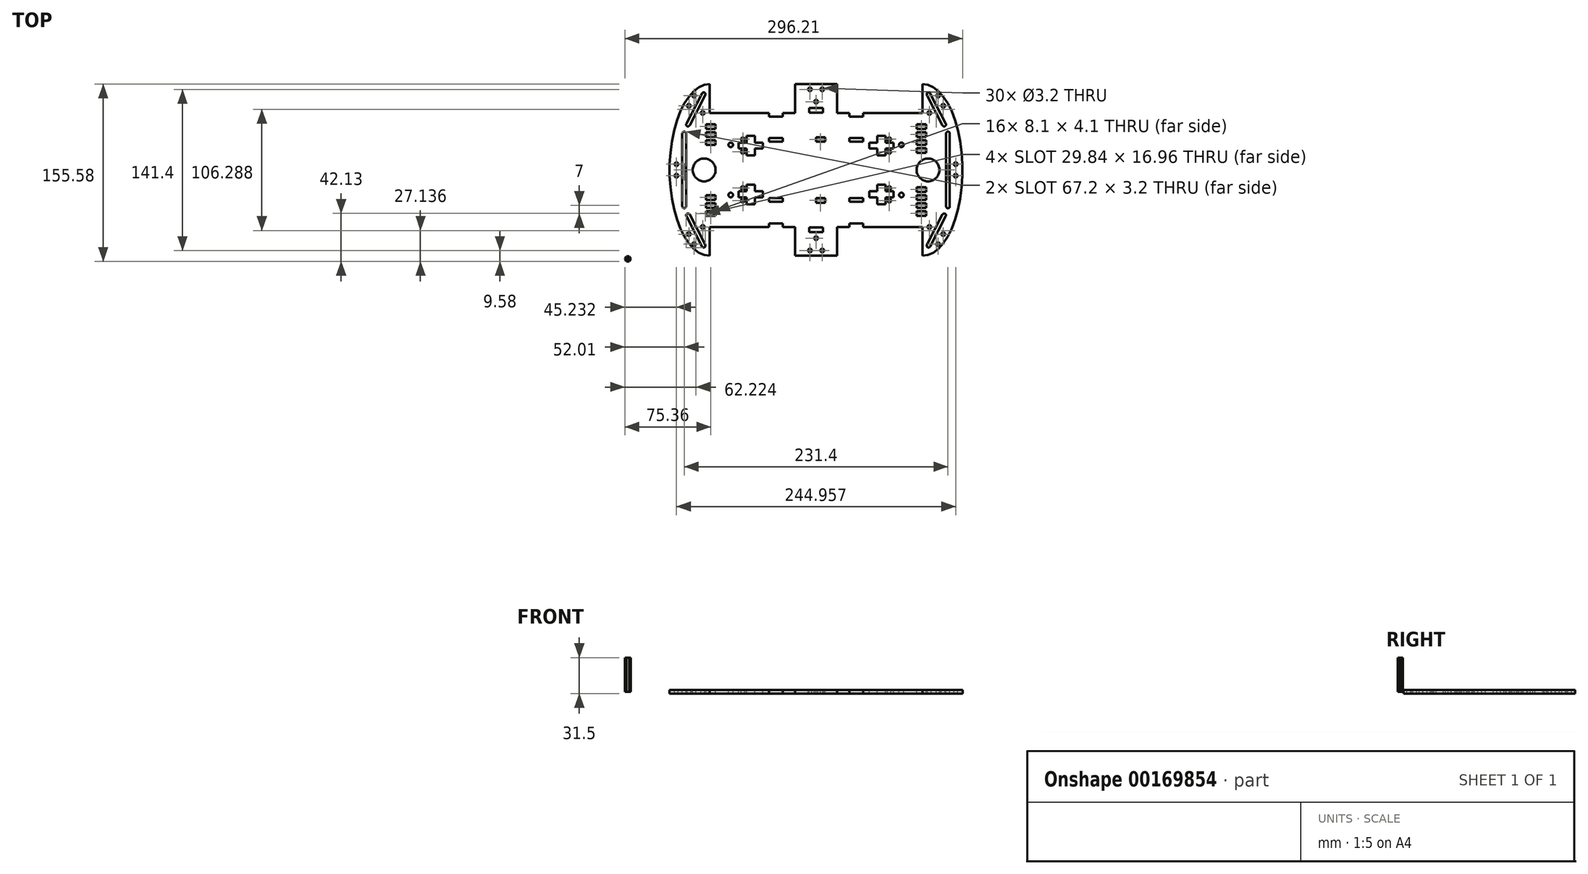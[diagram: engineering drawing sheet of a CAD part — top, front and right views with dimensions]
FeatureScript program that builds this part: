
annotation { "Feature Type Name" : "Feature", "Feature Type Description" : "" }
export const myFeature = defineFeature(function(context is Context, id is Id, definition is map)
    precondition{}
    {
        {
            var Q0;
            Q0=qCreatedBy(makeId("Top.planeOp"),FACE);
            var sketch = newSketch(context, id + "F0", { "sketchPlane" : qUnion([Q0])});
            skLineSegment(sketch, "E0", {"start": v(0, 75.3) * mm, "end": v(18.5, 75.3) * mm});
            skLineSegment(sketch, "E1", {"start": v(18.5, 75.3) * mm, "end": v(18.5, 50) * mm});
            skLineSegment(sketch, "E2", {"start": v(18.5, 50) * mm, "end": v(29.2, 50) * mm});
            skLineSegment(sketch, "E3", {"start": v(29.2, 50) * mm, "end": v(29.2, 46.8) * mm});
            skLineSegment(sketch, "E4", {"start": v(29.2, 46.8) * mm, "end": v(41.2, 46.8) * mm});
            skLineSegment(sketch, "E5", {"start": v(41.2, 46.8) * mm, "end": v(41.2, 50) * mm});
            skLineSegment(sketch, "E6", {"start": v(41.2, 50) * mm, "end": v(93.2, 50) * mm});
            skLineSegment(sketch, "E7", {"start": v(93.2, 50) * mm, "end": v(93.2, 75.3) * mm});
            skLineSegment(sketch, "E8", {"start": v(0, 116.08) * mm, "end": v(0, -110.3) * mm, "construction": true});
            skLineSegment(sketch, "E9", {"start": v(202.91, 0) * mm, "end": v(-192.77, 0) * mm, "construction": true});
            skEllipticalArc(sketch, "E10", {});
            skPoint(sketch, "E11", {"position": v(128.5, 0) * mm});
            skLineSegment(sketch, "E12.MirrorCS", {"start": v(0, -75.3) * mm, "end": v(18.5, -75.3) * mm});
            skLineSegment(sketch, "E13.MirrorCS", {"start": v(18.5, -75.3) * mm, "end": v(18.5, -50) * mm});
            skLineSegment(sketch, "E14.MirrorCS", {"start": v(18.5, -50) * mm, "end": v(29.2, -50) * mm});
            skLineSegment(sketch, "E15.MirrorCS", {"start": v(29.2, -50) * mm, "end": v(29.2, -46.8) * mm});
            skLineSegment(sketch, "E16.MirrorCS", {"start": v(29.2, -46.8) * mm, "end": v(41.2, -46.8) * mm});
            skLineSegment(sketch, "E17.MirrorCS", {"start": v(41.2, -46.8) * mm, "end": v(41.2, -50) * mm});
            skLineSegment(sketch, "E18.MirrorCS", {"start": v(41.2, -50) * mm, "end": v(93.2, -50) * mm});
            skEllipticalArc(sketch, "E19.MirrorCS", {});
            skLineSegment(sketch, "E20.MirrorCS", {"start": v(93.2, -50) * mm, "end": v(93.2, -75.3) * mm});
            skEllipticalArc(sketch, "E21.MirrorCS", {});
            skEllipticalArc(sketch, "E22.MirrorCS", {});
            skLineSegment(sketch, "E23.MirrorCS", {"start": v(-93.2, -50) * mm, "end": v(-93.2, -75.3) * mm});
            skLineSegment(sketch, "E24.MirrorCS", {"start": v(-41.2, -50) * mm, "end": v(-93.2, -50) * mm});
            skLineSegment(sketch, "E25.MirrorCS", {"start": v(-41.2, 50) * mm, "end": v(-93.2, 50) * mm});
            skLineSegment(sketch, "E26.MirrorCS", {"start": v(-29.2, 46.8) * mm, "end": v(-41.2, 46.8) * mm});
            skLineSegment(sketch, "E27.MirrorCS", {"start": v(-29.2, -46.8) * mm, "end": v(-41.2, -46.8) * mm});
            skLineSegment(sketch, "E28.MirrorCS", {"start": v(-18.5, -50) * mm, "end": v(-29.2, -50) * mm});
            skLineSegment(sketch, "E29.MirrorCS", {"start": v(-18.5, -75.3) * mm, "end": v(-18.5, -50) * mm});
            skLineSegment(sketch, "E30.MirrorCS", {"start": v(0, -75.3) * mm, "end": v(-18.5, -75.3) * mm});
            skLineSegment(sketch, "E31.MirrorCS", {"start": v(0, 75.3) * mm, "end": v(-18.5, 75.3) * mm});
            skLineSegment(sketch, "E32.MirrorCS", {"start": v(-18.5, 75.3) * mm, "end": v(-18.5, 50) * mm});
            skLineSegment(sketch, "E33.MirrorCS", {"start": v(-18.5, 50) * mm, "end": v(-29.2, 50) * mm});
            skLineSegment(sketch, "E34.MirrorCS", {"start": v(-93.2, 50) * mm, "end": v(-93.2, 75.3) * mm});
            skLineSegment(sketch, "E35.MirrorCS", {"start": v(-29.2, -50) * mm, "end": v(-29.2, -46.8) * mm});
            skLineSegment(sketch, "E36.MirrorCS", {"start": v(-41.2, -46.8) * mm, "end": v(-41.2, -50) * mm});
            skLineSegment(sketch, "E37.MirrorCS", {"start": v(-29.2, 50) * mm, "end": v(-29.2, 46.8) * mm});
            skLineSegment(sketch, "E38.MirrorCS", {"start": v(-41.2, 46.8) * mm, "end": v(-41.2, 50) * mm});
            const initialGuessF0  = {"E10": [0.0932, 0, 0, 1, 0.0753, 0.0353, 4.71238898038469, 0], "E19.MirrorCS": [0.0932, 0, 0, -1, 0.0753, 0.0353, 0, 1.5707963267948966], "E21.MirrorCS": [-0.0932, 0, 0, 1, 0.0753, 0.0353, 0, 1.5707963267948966], "E22.MirrorCS": [-0.0932, 0, 0, -1, 0.0753, 0.0353, 4.71238898038469, 0]};
            skSetInitialGuess(sketch, initialGuessF0);
            skSolve(sketch);
        }
        {
            var Q0;
            Q0 = qSketchRegion(id + "F0", true);
            extrude(context, id + "F1", {"entities" : qUnion([Q0]), "depth" : 3 * mm, "symmetric" : true});
        }
        {
            var Q0;
            Q0=makeQuery(id+"F1.opExtrude","CAP_FACE",FACE,{"disambiguationData":[OSD([sQuery(id+"F0.wireOp",EDGE,"E0"),sQuery(id+"F0.wireOp",EDGE,"E1"),sQuery(id+"F0.wireOp",EDGE,"E2"),sQuery(id+"F0.wireOp",EDGE,"E3"),sQuery(id+"F0.wireOp",EDGE,"E4"),sQuery(id+"F0.wireOp",EDGE,"E5"),sQuery(id+"F0.wireOp",EDGE,"E6"),sQuery(id+"F0.wireOp",EDGE,"E7"),sQuery(id+"F0.wireOp",EDGE,"E10"),sQuery(id+"F0.wireOp",EDGE,"E12.MirrorCS"),sQuery(id+"F0.wireOp",EDGE,"E13.MirrorCS"),sQuery(id+"F0.wireOp",EDGE,"E14.MirrorCS"),sQuery(id+"F0.wireOp",EDGE,"E15.MirrorCS"),sQuery(id+"F0.wireOp",EDGE,"E16.MirrorCS"),sQuery(id+"F0.wireOp",EDGE,"E17.MirrorCS"),sQuery(id+"F0.wireOp",EDGE,"E18.MirrorCS"),sQuery(id+"F0.wireOp",EDGE,"E19.MirrorCS"),sQuery(id+"F0.wireOp",EDGE,"E20.MirrorCS"),sQuery(id+"F0.wireOp",EDGE,"E21.MirrorCS"),sQuery(id+"F0.wireOp",EDGE,"E22.MirrorCS"),sQuery(id+"F0.wireOp",EDGE,"E23.MirrorCS"),sQuery(id+"F0.wireOp",EDGE,"E24.MirrorCS"),sQuery(id+"F0.wireOp",EDGE,"E25.MirrorCS"),sQuery(id+"F0.wireOp",EDGE,"E26.MirrorCS"),sQuery(id+"F0.wireOp",EDGE,"E27.MirrorCS"),sQuery(id+"F0.wireOp",EDGE,"E28.MirrorCS"),sQuery(id+"F0.wireOp",EDGE,"E29.MirrorCS"),sQuery(id+"F0.wireOp",EDGE,"E30.MirrorCS"),sQuery(id+"F0.wireOp",EDGE,"E31.MirrorCS"),sQuery(id+"F0.wireOp",EDGE,"E32.MirrorCS"),sQuery(id+"F0.wireOp",EDGE,"E33.MirrorCS"),sQuery(id+"F0.wireOp",EDGE,"E34.MirrorCS"),sQuery(id+"F0.wireOp",EDGE,"E35.MirrorCS"),sQuery(id+"F0.wireOp",EDGE,"E36.MirrorCS"),sQuery(id+"F0.wireOp",EDGE,"E37.MirrorCS"),sQuery(id+"F0.wireOp",EDGE,"E38.MirrorCS")])],"isStart":false});
            var sketch = newSketch(context, id + "F2", { "sketchPlane" : qUnion([Q0])});
            skLineSegment(sketch, "E39", {"start": v(-128.5, 0) * mm, "end": v(128.5, 0) * mm, "construction": true});
            skLineSegment(sketch, "E40", {"start": v(93.2, 50) * mm, "end": v(93.2, -50) * mm, "construction": true});
            skLineSegment(sketch, "E41", {"start": v(-93.2, 50) * mm, "end": v(-93.2, -50) * mm, "construction": true});
            skCircle(sketch, "E42", {"center": v(0, 59.9) * mm, "radius": 1.6 * mm});
            skCircle(sketch, "E43", {"center": v(5.4, 70.7) * mm, "radius": 1.6 * mm});
            skLineSegment(sketch, "E44.bottom", {"start": v(-6, 54.4) * mm, "end": v(6, 54.4) * mm});
            skLineSegment(sketch, "E44.top", {"start": v(-6, 50.3) * mm, "end": v(6, 50.3) * mm});
            skLineSegment(sketch, "E44.left", {"start": v(-6, 54.4) * mm, "end": v(-6, 50.3) * mm});
            skLineSegment(sketch, "E44.right", {"start": v(6, 54.4) * mm, "end": v(6, 50.3) * mm});
            skLineSegment(sketch, "E45.bottom", {"start": v(29.23, 28) * mm, "end": v(41.23, 28) * mm});
            skLineSegment(sketch, "E45.top", {"start": v(29.23, 24.8) * mm, "end": v(41.23, 24.8) * mm});
            skLineSegment(sketch, "E45.left", {"start": v(29.23, 28) * mm, "end": v(29.23, 24.8) * mm});
            skLineSegment(sketch, "E45.right", {"start": v(41.23, 28) * mm, "end": v(41.23, 24.8) * mm});
            skLineSegment(sketch, "E46.bottom", {"start": v(46.73, 24) * mm, "end": v(53.73, 24) * mm});
            skLineSegment(sketch, "E46.top", {"start": v(46.73, 18.8) * mm, "end": v(53.73, 18.8) * mm});
            skLineSegment(sketch, "E46.left", {"start": v(46.73, 24) * mm, "end": v(46.73, 18.8) * mm});
            skLineSegment(sketch, "E46.right", {"start": v(67.83, 24) * mm, "end": v(67.83, 18.8) * mm});
            skLineSegment(sketch, "E47.bottom", {"start": v(53.73, 30) * mm, "end": v(60.83, 30) * mm});
            skLineSegment(sketch, "E47.top", {"start": v(53.73, 12.8) * mm, "end": v(60.83, 12.8) * mm});
            skLineSegment(sketch, "E47.left", {"start": v(53.73, 30) * mm, "end": v(53.73, 24) * mm});
            skLineSegment(sketch, "E47.right", {"start": v(60.83, 30) * mm, "end": v(60.83, 24) * mm});
            skLineSegment(sketch, "E48", {"start": v(46.73, 21.4) * mm, "end": v(67.83, 21.4) * mm, "construction": true});
            skLineSegment(sketch, "E49", {"start": v(57.28, 30) * mm, "end": v(57.28, 12.8) * mm, "construction": true});
            skPoint(sketch, "E50", {"position": v(57.28, 21.4) * mm});
            skLineSegment(sketch, "E51.trimOffspring", {"start": v(60.83, 24) * mm, "end": v(67.83, 24) * mm});
            skLineSegment(sketch, "E52.trimOffspring", {"start": v(53.73, 18.8) * mm, "end": v(53.73, 12.8) * mm});
            skLineSegment(sketch, "E53.trimOffspring", {"start": v(60.83, 18.8) * mm, "end": v(67.83, 18.8) * mm});
            skLineSegment(sketch, "E54.trimOffspring", {"start": v(60.83, 18.8) * mm, "end": v(60.83, 12.8) * mm});
            skCircle(sketch, "E55", {"center": v(64.23, 26.9) * mm, "radius": 1.6 * mm});
            skLineSegment(sketch, "E56", {"start": v(35.2, 46.8) * mm, "end": v(35.2, 28) * mm, "construction": true});
            skPoint(sketch, "E56.endSnap0", {"position": v(35.23, 28) * mm});
            skCircle(sketch, "E57.MirrorC", {"center": v(64.23, 15.9) * mm, "radius": 1.6 * mm});
            skPoint(sketch, "E58", {"position": v(0, 54.4) * mm});
            skCircle(sketch, "E59.MirrorC", {"center": v(-5.4, 70.7) * mm, "radius": 1.6 * mm});
            skLineSegment(sketch, "E60.MirrorCS", {"start": v(-41.23, 28) * mm, "end": v(-41.23, 24.8) * mm});
            skLineSegment(sketch, "E61.MirrorCS", {"start": v(-29.23, 28) * mm, "end": v(-29.23, 24.8) * mm});
            skLineSegment(sketch, "E62.MirrorCS", {"start": v(-53.73, 18.8) * mm, "end": v(-53.73, 12.8) * mm});
            skLineSegment(sketch, "E63.MirrorCS", {"start": v(-67.83, 24) * mm, "end": v(-67.83, 18.8) * mm});
            skLineSegment(sketch, "E64.MirrorCS", {"start": v(-60.83, 18.8) * mm, "end": v(-60.83, 12.8) * mm});
            skLineSegment(sketch, "E65.MirrorCS", {"start": v(-53.73, 30) * mm, "end": v(-53.73, 24) * mm});
            skLineSegment(sketch, "E66.MirrorCS", {"start": v(-60.83, 30) * mm, "end": v(-60.83, 24) * mm});
            skLineSegment(sketch, "E67.MirrorCS", {"start": v(-46.73, 24) * mm, "end": v(-46.73, 18.8) * mm});
            skLineSegment(sketch, "E68.MirrorCS", {"start": v(-46.73, 24) * mm, "end": v(-53.73, 24) * mm});
            skLineSegment(sketch, "E69.MirrorCS", {"start": v(-53.73, 12.8) * mm, "end": v(-60.83, 12.8) * mm});
            skPoint(sketch, "E70.MirrorP", {"position": v(-57.28, 21.4) * mm});
            skCircle(sketch, "E71.MirrorC", {"center": v(-64.23, 26.9) * mm, "radius": 1.6 * mm});
            skLineSegment(sketch, "E72.MirrorCS", {"start": v(-29.23, 28) * mm, "end": v(-41.23, 28) * mm});
            skLineSegment(sketch, "E73.MirrorCS", {"start": v(-29.23, 24.8) * mm, "end": v(-41.23, 24.8) * mm});
            skCircle(sketch, "E74.MirrorC", {"center": v(-64.23, 15.9) * mm, "radius": 1.6 * mm});
            skLineSegment(sketch, "E75.MirrorCS", {"start": v(-53.73, 30) * mm, "end": v(-60.83, 30) * mm});
            skPoint(sketch, "E76.MirrorP", {"position": v(-35.23, 28) * mm});
            skLineSegment(sketch, "E77.MirrorCS", {"start": v(-60.83, 18.8) * mm, "end": v(-67.83, 18.8) * mm});
            skLineSegment(sketch, "E78.MirrorCS", {"start": v(-60.83, 24) * mm, "end": v(-67.83, 24) * mm});
            skLineSegment(sketch, "E79.MirrorCS", {"start": v(-46.73, 18.8) * mm, "end": v(-53.73, 18.8) * mm});
            skLineSegment(sketch, "E80.MirrorCS", {"start": v(-67.83, -24) * mm, "end": v(-67.83, -18.8) * mm});
            skLineSegment(sketch, "E81.MirrorCS", {"start": v(29.23, -28) * mm, "end": v(29.23, -24.8) * mm});
            skLineSegment(sketch, "E82.MirrorCS", {"start": v(-53.73, -12.8) * mm, "end": v(-60.83, -12.8) * mm});
            skLineSegment(sketch, "E83.MirrorCS", {"start": v(-46.73, -24) * mm, "end": v(-46.73, -18.8) * mm});
            skLineSegment(sketch, "E84.MirrorCS", {"start": v(-41.23, -28) * mm, "end": v(-41.23, -24.8) * mm});
            skLineSegment(sketch, "E85.MirrorCS", {"start": v(41.23, -28) * mm, "end": v(41.23, -24.8) * mm});
            skLineSegment(sketch, "E86.MirrorCS", {"start": v(-53.73, -30) * mm, "end": v(-60.83, -30) * mm});
            skLineSegment(sketch, "E87.MirrorCS", {"start": v(-29.23, -28) * mm, "end": v(-29.23, -24.8) * mm});
            skLineSegment(sketch, "E88.MirrorCS", {"start": v(53.73, -12.8) * mm, "end": v(60.83, -12.8) * mm});
            skPoint(sketch, "E89.MirrorP", {"position": v(-57.28, -21.4) * mm});
            skLineSegment(sketch, "E90.MirrorCS", {"start": v(53.73, -30) * mm, "end": v(60.83, -30) * mm});
            skLineSegment(sketch, "E91.MirrorCS", {"start": v(67.83, -24) * mm, "end": v(67.83, -18.8) * mm});
            skLineSegment(sketch, "E92.MirrorCS", {"start": v(46.73, -24) * mm, "end": v(46.73, -18.8) * mm});
            skPoint(sketch, "E93.MirrorP", {"position": v(57.28, -21.4) * mm});
            skLineSegment(sketch, "E94.MirrorCS", {"start": v(46.73, -24) * mm, "end": v(53.73, -24) * mm});
            skLineSegment(sketch, "E95.MirrorCS", {"start": v(-29.23, -28) * mm, "end": v(-41.23, -28) * mm});
            skLineSegment(sketch, "E96.MirrorCS", {"start": v(60.83, -18.8) * mm, "end": v(60.83, -12.8) * mm});
            skLineSegment(sketch, "E97.MirrorCS", {"start": v(60.83, -18.8) * mm, "end": v(67.83, -18.8) * mm});
            skCircle(sketch, "E98.MirrorC", {"center": v(-64.23, -26.9) * mm, "radius": 1.6 * mm});
            skLineSegment(sketch, "E99.MirrorCS", {"start": v(-46.73, -18.8) * mm, "end": v(-53.73, -18.8) * mm});
            skLineSegment(sketch, "E100.MirrorCS", {"start": v(-53.73, -18.8) * mm, "end": v(-53.73, -12.8) * mm});
            skLineSegment(sketch, "E101.MirrorCS", {"start": v(-60.83, -30) * mm, "end": v(-60.83, -24) * mm});
            skLineSegment(sketch, "E102.MirrorCS", {"start": v(53.73, -18.8) * mm, "end": v(53.73, -12.8) * mm});
            skLineSegment(sketch, "E103.MirrorCS", {"start": v(29.23, -24.8) * mm, "end": v(41.23, -24.8) * mm});
            skLineSegment(sketch, "E104.MirrorCS", {"start": v(29.23, -28) * mm, "end": v(41.23, -28) * mm});
            skLineSegment(sketch, "E105.MirrorCS", {"start": v(-60.83, -18.8) * mm, "end": v(-67.83, -18.8) * mm});
            skCircle(sketch, "E106.MirrorC", {"center": v(-64.23, -15.9) * mm, "radius": 1.6 * mm});
            skLineSegment(sketch, "E107.MirrorCS", {"start": v(53.73, -30) * mm, "end": v(53.73, -24) * mm});
            skLineSegment(sketch, "E108.MirrorCS", {"start": v(-60.83, -18.8) * mm, "end": v(-60.83, -12.8) * mm});
            skLineSegment(sketch, "E109.MirrorCS", {"start": v(46.73, -18.8) * mm, "end": v(53.73, -18.8) * mm});
            skPoint(sketch, "E110.MirrorP", {"position": v(-35.23, -28) * mm});
            skLineSegment(sketch, "E111.MirrorCS", {"start": v(60.83, -30) * mm, "end": v(60.83, -24) * mm});
            skCircle(sketch, "E112.MirrorC", {"center": v(64.23, -15.9) * mm, "radius": 1.6 * mm});
            skLineSegment(sketch, "E113.MirrorCS", {"start": v(60.83, -24) * mm, "end": v(67.83, -24) * mm});
            skLineSegment(sketch, "E114.MirrorCS", {"start": v(-46.73, -24) * mm, "end": v(-53.73, -24) * mm});
            skLineSegment(sketch, "E115.MirrorCS", {"start": v(-53.73, -30) * mm, "end": v(-53.73, -24) * mm});
            skCircle(sketch, "E116.MirrorC", {"center": v(64.23, -26.9) * mm, "radius": 1.6 * mm});
            skPoint(sketch, "E117.MirrorP", {"position": v(35.23, -28) * mm});
            skLineSegment(sketch, "E118.MirrorCS", {"start": v(-29.23, -24.8) * mm, "end": v(-41.23, -24.8) * mm});
            skLineSegment(sketch, "E119.MirrorCS", {"start": v(0, -75.3) * mm, "end": v(0, 75.3) * mm, "construction": true});
            skLineSegment(sketch, "E120.MirrorCS", {"start": v(-60.83, -24) * mm, "end": v(-67.83, -24) * mm});
            skLineSegment(sketch, "E121.MirrorCS", {"start": v(6, -54.4) * mm, "end": v(6, -50.3) * mm});
            skLineSegment(sketch, "E122.MirrorCS", {"start": v(-6, -54.4) * mm, "end": v(-6, -50.3) * mm});
            skLineSegment(sketch, "E123.MirrorCS", {"start": v(-6, -54.4) * mm, "end": v(6, -54.4) * mm});
            skCircle(sketch, "E124.MirrorC", {"center": v(5.4, -70.7) * mm, "radius": 1.6 * mm});
            skCircle(sketch, "E125.MirrorC", {"center": v(0, -59.9) * mm, "radius": 1.6 * mm});
            skCircle(sketch, "E126.MirrorC", {"center": v(-5.4, -70.7) * mm, "radius": 1.6 * mm});
            skPoint(sketch, "E127.MirrorP", {"position": v(0, -54.4) * mm});
            skLineSegment(sketch, "E128.MirrorCS", {"start": v(-6, -50.3) * mm, "end": v(6, -50.3) * mm});
            skCircle(sketch, "E129", {"center": v(98.2, 0) * mm, "radius": 10 * mm});
            skPoint(sketch, "E130", {"position": v(93.2, 0) * mm});
            skLineSegment(sketch, "E131", {"start": v(114.1, 32) * mm, "end": v(114.1, -32) * mm});
            skLineSegment(sketch, "E132", {"start": v(117.3, -32) * mm, "end": v(117.3, 32) * mm});
            skArc(sketch, "E133", {"start": v(114.1, 32) * mm, "mid": v(115.7, 33.6) * mm, "end": v(117.3, 32) * mm});
            skArc(sketch, "E134", {"start": v(114.1, -32) * mm, "mid": v(115.7, -33.6) * mm, "end": v(117.3, -32) * mm});
            skPoint(sketch, "E135", {"position": v(114.1, 0) * mm});
            skLineSegment(sketch, "E136", {"start": v(110.95, -39.08) * mm, "end": v(97.18, -65.74) * mm});
            skLineSegment(sketch, "E137", {"start": v(100.02, -67.2) * mm, "end": v(113.8, -40.55) * mm});
            skArc(sketch, "E138", {"start": v(110.95, -39.08) * mm, "mid": v(113.1, -38.4) * mm, "end": v(113.8, -40.55) * mm});
            skArc(sketch, "E139", {"start": v(97.18, -65.74) * mm, "mid": v(97.87, -67.9) * mm, "end": v(100.02, -67.2) * mm});
            skCircle(sketch, "E140.MirrorC", {"center": v(99.4, -50) * mm, "radius": 1.6 * mm});
            skLineSegment(sketch, "E141.MirrorCS", {"start": v(-117.3, -32) * mm, "end": v(-117.3, 32) * mm});
            skLineSegment(sketch, "E142.MirrorCS", {"start": v(-114.1, 32) * mm, "end": v(-114.1, -32) * mm});
            skArc(sketch, "E143.MirrorCS", {"start": v(-114.1, 32) * mm, "mid": v(-115.7, 33.6) * mm, "end": v(-117.3, 32) * mm});
            skArc(sketch, "E144.MirrorCS", {"start": v(-114.1, -32) * mm, "mid": v(-115.7, -33.6) * mm, "end": v(-117.3, -32) * mm});
            skCircle(sketch, "E145", {"center": v(122.48, 5.05) * mm, "radius": 1.6 * mm});
            skCircle(sketch, "E146.MirrorC", {"center": v(122.48, -5.05) * mm, "radius": 1.6 * mm});
            skCircle(sketch, "E147.MirrorC", {"center": v(-122.48, 5.05) * mm, "radius": 1.6 * mm});
            skCircle(sketch, "E148.MirrorC", {"center": v(-122.48, -5.05) * mm, "radius": 1.6 * mm});
            skLineSegment(sketch, "E149", {"start": v(120.35, -60.82) * mm, "end": v(90.96, -45.64) * mm, "construction": true});
            skPoint(sketch, "E150", {"position": v(104.06, -52.4) * mm});
            skLineSegment(sketch, "E151", {"start": v(93.2, -50) * mm, "end": v(99.4, -50) * mm, "construction": true});
            skLineSegment(sketch, "E152", {"start": v(112.37, -39.82) * mm, "end": v(98.6, -66.47) * mm, "construction": true});
            skCircle(sketch, "E153.MirrorC", {"center": v(111.57, -56.29) * mm, "radius": 1.6 * mm});
            skCircle(sketch, "E154", {"center": v(106.98, -65.17) * mm, "radius": 1.6 * mm});
            skLineSegment(sketch, "E155", {"start": v(111.57, -56.29) * mm, "end": v(107.23, -64.7) * mm, "construction": true});
            skLineSegment(sketch, "E156.MirrorCS", {"start": v(100.02, 67.2) * mm, "end": v(113.8, 40.55) * mm});
            skLineSegment(sketch, "E157.MirrorCS", {"start": v(110.95, 39.08) * mm, "end": v(97.18, 65.74) * mm});
            skArc(sketch, "E158.MirrorCS", {"start": v(110.95, 39.08) * mm, "mid": v(113.1, 38.4) * mm, "end": v(113.8, 40.55) * mm});
            skArc(sketch, "E159.MirrorCS", {"start": v(97.18, 65.74) * mm, "mid": v(97.87, 67.9) * mm, "end": v(100.02, 67.2) * mm});
            skCircle(sketch, "E160.MirrorC", {"center": v(99.4, 50) * mm, "radius": 1.6 * mm});
            skCircle(sketch, "E161.MirrorC", {"center": v(111.57, 56.29) * mm, "radius": 1.6 * mm});
            skCircle(sketch, "E162.MirrorC", {"center": v(106.98, 65.17) * mm, "radius": 1.6 * mm});
            skCircle(sketch, "E163.MirrorC", {"center": v(-111.57, 56.29) * mm, "radius": 1.6 * mm});
            skLineSegment(sketch, "E164.MirrorCS", {"start": v(-100.02, 67.2) * mm, "end": v(-113.8, 40.55) * mm});
            skLineSegment(sketch, "E165.MirrorCS", {"start": v(-110.95, 39.08) * mm, "end": v(-97.18, 65.74) * mm});
            skCircle(sketch, "E166.MirrorC", {"center": v(-99.4, 50) * mm, "radius": 1.6 * mm});
            skCircle(sketch, "E167.MirrorC", {"center": v(-106.98, 65.17) * mm, "radius": 1.6 * mm});
            skArc(sketch, "E168.MirrorCS", {"start": v(-110.95, 39.08) * mm, "mid": v(-113.1, 38.4) * mm, "end": v(-113.8, 40.55) * mm});
            skArc(sketch, "E169.MirrorCS", {"start": v(-97.18, 65.74) * mm, "mid": v(-97.87, 67.9) * mm, "end": v(-100.02, 67.2) * mm});
            skCircle(sketch, "E170.MirrorC", {"center": v(-111.57, -56.29) * mm, "radius": 1.6 * mm});
            skCircle(sketch, "E171.MirrorC", {"center": v(-106.98, -65.17) * mm, "radius": 1.6 * mm});
            skCircle(sketch, "E172.MirrorC", {"center": v(-99.4, -50) * mm, "radius": 1.6 * mm});
            skLineSegment(sketch, "E173.MirrorCS", {"start": v(-110.95, -39.08) * mm, "end": v(-97.18, -65.74) * mm});
            skLineSegment(sketch, "E174.MirrorCS", {"start": v(-100.02, -67.2) * mm, "end": v(-113.8, -40.55) * mm});
            skArc(sketch, "E175.MirrorCS", {"start": v(-110.95, -39.08) * mm, "mid": v(-113.1, -38.4) * mm, "end": v(-113.8, -40.55) * mm});
            skArc(sketch, "E176.MirrorCS", {"start": v(-97.18, -65.74) * mm, "mid": v(-97.87, -67.9) * mm, "end": v(-100.02, -67.2) * mm});
            skCircle(sketch, "E177", {"center": v(74.83, -22) * mm, "radius": 2 * mm});
            skLineSegment(sketch, "E178.bottom", {"start": v(88.3, -36.1) * mm, "end": v(96.4, -36.1) * mm});
            skLineSegment(sketch, "E178.top", {"start": v(88.3, -40.2) * mm, "end": v(96.4, -40.2) * mm});
            skLineSegment(sketch, "E178.left", {"start": v(88.3, -36.1) * mm, "end": v(88.3, -40.2) * mm});
            skLineSegment(sketch, "E178.right", {"start": v(96.4, -36.1) * mm, "end": v(96.4, -40.2) * mm});
            skCircle(sketch, "E179.MirrorC", {"center": v(-74.83, -22) * mm, "radius": 2 * mm});
            skCircle(sketch, "E180.MirrorC", {"center": v(74.83, 22) * mm, "radius": 2 * mm});
            skCircle(sketch, "E181.MirrorC", {"center": v(-74.83, 22) * mm, "radius": 2 * mm});
            skLineSegment(sketch, "E182", {"start": v(67.83, -24) * mm, "end": v(76, -24) * mm, "construction": true});
            skLineSegment(sketch, "E183.1.0.0", {"start": v(88.3, -33.2) * mm, "end": v(96.4, -33.2) * mm});
            skLineSegment(sketch, "E183.1.0.1", {"start": v(88.3, -29.1) * mm, "end": v(88.3, -33.2) * mm});
            skLineSegment(sketch, "E183.1.0.2", {"start": v(88.3, -29.1) * mm, "end": v(96.4, -29.1) * mm});
            skLineSegment(sketch, "E183.1.0.3", {"start": v(96.4, -29.1) * mm, "end": v(96.4, -33.2) * mm});
            skLineSegment(sketch, "E183.2.0.0", {"start": v(88.3, -26.2) * mm, "end": v(96.4, -26.2) * mm});
            skLineSegment(sketch, "E183.2.0.1", {"start": v(88.3, -22.1) * mm, "end": v(88.3, -26.2) * mm});
            skLineSegment(sketch, "E183.2.0.2", {"start": v(88.3, -22.1) * mm, "end": v(96.4, -22.1) * mm});
            skLineSegment(sketch, "E183.2.0.3", {"start": v(96.4, -22.1) * mm, "end": v(96.4, -26.2) * mm});
            skLineSegment(sketch, "E183.direction1", {"start": v(88.3, -40.2) * mm, "end": v(88.3, -33.2) * mm, "construction": true});
            skLineSegment(sketch, "E184.MirrorCS", {"start": v(-88.3, -22.1) * mm, "end": v(-96.4, -22.1) * mm});
            skLineSegment(sketch, "E185.MirrorCS", {"start": v(-88.3, -22.1) * mm, "end": v(-88.3, -26.2) * mm});
            skLineSegment(sketch, "E186.MirrorCS", {"start": v(-96.4, -22.1) * mm, "end": v(-96.4, -26.2) * mm});
            skLineSegment(sketch, "E187.MirrorCS", {"start": v(-88.3, -26.2) * mm, "end": v(-96.4, -26.2) * mm});
            skLineSegment(sketch, "E188.MirrorCS", {"start": v(-88.3, -29.1) * mm, "end": v(-96.4, -29.1) * mm});
            skLineSegment(sketch, "E189.MirrorCS", {"start": v(-96.4, -29.1) * mm, "end": v(-96.4, -33.2) * mm});
            skLineSegment(sketch, "E190.MirrorCS", {"start": v(-88.3, -29.1) * mm, "end": v(-88.3, -33.2) * mm});
            skLineSegment(sketch, "E191.MirrorCS", {"start": v(-88.3, -33.2) * mm, "end": v(-96.4, -33.2) * mm});
            skLineSegment(sketch, "E192.MirrorCS", {"start": v(-88.3, -36.1) * mm, "end": v(-96.4, -36.1) * mm});
            skLineSegment(sketch, "E193.MirrorCS", {"start": v(-88.3, -40.2) * mm, "end": v(-88.3, -33.2) * mm, "construction": true});
            skLineSegment(sketch, "E194.MirrorCS", {"start": v(-96.4, -36.1) * mm, "end": v(-96.4, -40.2) * mm});
            skLineSegment(sketch, "E195.MirrorCS", {"start": v(-88.3, -40.2) * mm, "end": v(-96.4, -40.2) * mm});
            skLineSegment(sketch, "E196.MirrorCS", {"start": v(-88.3, -36.1) * mm, "end": v(-88.3, -40.2) * mm});
            skLineSegment(sketch, "E197.MirrorCS", {"start": v(-88.3, 36.1) * mm, "end": v(-88.3, 40.2) * mm});
            skLineSegment(sketch, "E198.MirrorCS", {"start": v(-88.3, 40.2) * mm, "end": v(-88.3, 33.2) * mm, "construction": true});
            skLineSegment(sketch, "E199.MirrorCS", {"start": v(-96.4, 29.1) * mm, "end": v(-96.4, 33.2) * mm});
            skLineSegment(sketch, "E200.MirrorCS", {"start": v(-96.4, 36.1) * mm, "end": v(-96.4, 40.2) * mm});
            skLineSegment(sketch, "E201.MirrorCS", {"start": v(-96.4, 22.1) * mm, "end": v(-96.4, 26.2) * mm});
            skLineSegment(sketch, "E202.MirrorCS", {"start": v(-88.3, 22.1) * mm, "end": v(-96.4, 22.1) * mm});
            skLineSegment(sketch, "E203.MirrorCS", {"start": v(-88.3, 33.2) * mm, "end": v(-96.4, 33.2) * mm});
            skLineSegment(sketch, "E204.MirrorCS", {"start": v(-88.3, 40.2) * mm, "end": v(-96.4, 40.2) * mm});
            skLineSegment(sketch, "E205.MirrorCS", {"start": v(-88.3, 36.1) * mm, "end": v(-96.4, 36.1) * mm});
            skLineSegment(sketch, "E206.MirrorCS", {"start": v(-88.3, 29.1) * mm, "end": v(-96.4, 29.1) * mm});
            skLineSegment(sketch, "E207.MirrorCS", {"start": v(-88.3, 29.1) * mm, "end": v(-88.3, 33.2) * mm});
            skLineSegment(sketch, "E208.MirrorCS", {"start": v(-88.3, 26.2) * mm, "end": v(-96.4, 26.2) * mm});
            skLineSegment(sketch, "E209.MirrorCS", {"start": v(-88.3, 22.1) * mm, "end": v(-88.3, 26.2) * mm});
            skLineSegment(sketch, "E210.MirrorCS", {"start": v(88.3, 36.1) * mm, "end": v(88.3, 40.2) * mm});
            skLineSegment(sketch, "E211.MirrorCS", {"start": v(88.3, 36.1) * mm, "end": v(96.4, 36.1) * mm});
            skLineSegment(sketch, "E212.MirrorCS", {"start": v(96.4, 22.1) * mm, "end": v(96.4, 26.2) * mm});
            skLineSegment(sketch, "E213.MirrorCS", {"start": v(96.4, 36.1) * mm, "end": v(96.4, 40.2) * mm});
            skLineSegment(sketch, "E214.MirrorCS", {"start": v(88.3, 22.1) * mm, "end": v(88.3, 26.2) * mm});
            skLineSegment(sketch, "E215.MirrorCS", {"start": v(88.3, 33.2) * mm, "end": v(96.4, 33.2) * mm});
            skLineSegment(sketch, "E216.MirrorCS", {"start": v(88.3, 29.1) * mm, "end": v(96.4, 29.1) * mm});
            skLineSegment(sketch, "E217.MirrorCS", {"start": v(88.3, 29.1) * mm, "end": v(88.3, 33.2) * mm});
            skLineSegment(sketch, "E218.MirrorCS", {"start": v(96.4, 29.1) * mm, "end": v(96.4, 33.2) * mm});
            skLineSegment(sketch, "E219.MirrorCS", {"start": v(88.3, 40.2) * mm, "end": v(88.3, 33.2) * mm, "construction": true});
            skLineSegment(sketch, "E220.MirrorCS", {"start": v(88.3, 40.2) * mm, "end": v(96.4, 40.2) * mm});
            skLineSegment(sketch, "E221.MirrorCS", {"start": v(88.3, 26.2) * mm, "end": v(96.4, 26.2) * mm});
            skLineSegment(sketch, "E222.MirrorCS", {"start": v(88.3, 22.1) * mm, "end": v(96.4, 22.1) * mm});
            skCircle(sketch, "E223.MirrorC", {"center": v(-98.2, 0) * mm, "radius": 10 * mm});
            skSolve(sketch);
        }
        {
            var Q0;
            Q0 = qSketchRegion(id + "F2", true);
            extrude(context, id + "F3", {"entities" : qUnion([Q0]), "operationType" : NewBodyOperationType.REMOVE, "endBound" : BoundingType.UP_TO_NEXT, "oppositeDirection" : true, "depth" : 25 * mm});
        }
        {
            var Q0;
            Q0=makeQuery(id+"F1.opExtrude","CAP_FACE",FACE,{"disambiguationData":[OSD([sQuery(id+"F0.wireOp",EDGE,"E0"),sQuery(id+"F0.wireOp",EDGE,"E1"),sQuery(id+"F0.wireOp",EDGE,"E2"),sQuery(id+"F0.wireOp",EDGE,"E3"),sQuery(id+"F0.wireOp",EDGE,"E4"),sQuery(id+"F0.wireOp",EDGE,"E5"),sQuery(id+"F0.wireOp",EDGE,"E6"),sQuery(id+"F0.wireOp",EDGE,"E7"),sQuery(id+"F0.wireOp",EDGE,"E10"),sQuery(id+"F0.wireOp",EDGE,"E12.MirrorCS"),sQuery(id+"F0.wireOp",EDGE,"E13.MirrorCS"),sQuery(id+"F0.wireOp",EDGE,"E14.MirrorCS"),sQuery(id+"F0.wireOp",EDGE,"E15.MirrorCS"),sQuery(id+"F0.wireOp",EDGE,"E16.MirrorCS"),sQuery(id+"F0.wireOp",EDGE,"E17.MirrorCS"),sQuery(id+"F0.wireOp",EDGE,"E18.MirrorCS"),sQuery(id+"F0.wireOp",EDGE,"E19.MirrorCS"),sQuery(id+"F0.wireOp",EDGE,"E20.MirrorCS"),sQuery(id+"F0.wireOp",EDGE,"E21.MirrorCS"),sQuery(id+"F0.wireOp",EDGE,"E22.MirrorCS"),sQuery(id+"F0.wireOp",EDGE,"E23.MirrorCS"),sQuery(id+"F0.wireOp",EDGE,"E24.MirrorCS"),sQuery(id+"F0.wireOp",EDGE,"E25.MirrorCS"),sQuery(id+"F0.wireOp",EDGE,"E26.MirrorCS"),sQuery(id+"F0.wireOp",EDGE,"E27.MirrorCS"),sQuery(id+"F0.wireOp",EDGE,"E28.MirrorCS"),sQuery(id+"F0.wireOp",EDGE,"E29.MirrorCS"),sQuery(id+"F0.wireOp",EDGE,"E30.MirrorCS"),sQuery(id+"F0.wireOp",EDGE,"E31.MirrorCS"),sQuery(id+"F0.wireOp",EDGE,"E32.MirrorCS"),sQuery(id+"F0.wireOp",EDGE,"E33.MirrorCS"),sQuery(id+"F0.wireOp",EDGE,"E34.MirrorCS"),sQuery(id+"F0.wireOp",EDGE,"E35.MirrorCS"),sQuery(id+"F0.wireOp",EDGE,"E36.MirrorCS"),sQuery(id+"F0.wireOp",EDGE,"E37.MirrorCS"),sQuery(id+"F0.wireOp",EDGE,"E38.MirrorCS")])],"isStart":false});
            var sketch = newSketch(context, id + "F4", { "sketchPlane" : qUnion([Q0])});
            skLineSegment(sketch, "E224.bottom", {"start": v(-0.1, -24.7) * mm, "end": v(8, -24.7) * mm});
            skLineSegment(sketch, "E224.top", {"start": v(-0.1, -28.8) * mm, "end": v(8, -28.8) * mm});
            skLineSegment(sketch, "E224.left", {"start": v(-0.1, -24.7) * mm, "end": v(-0.1, -28.8) * mm});
            skLineSegment(sketch, "E224.right", {"start": v(8, -24.7) * mm, "end": v(8, -28.8) * mm});
            skLineSegment(sketch, "E225", {"start": v(-128.5, 0) * mm, "end": v(128.5, 0) * mm});
            skLineSegment(sketch, "E226.MirrorCS", {"start": v(8, 24.7) * mm, "end": v(8, 28.8) * mm});
            skLineSegment(sketch, "E227.MirrorCS", {"start": v(-0.1, 24.7) * mm, "end": v(-0.1, 28.8) * mm});
            skLineSegment(sketch, "E228.MirrorCS", {"start": v(-0.1, 28.8) * mm, "end": v(8, 28.8) * mm});
            skLineSegment(sketch, "E229.MirrorCS", {"start": v(-0.1, 24.7) * mm, "end": v(8, 24.7) * mm});
            skLineSegment(sketch, "E230.bottom", {"start": v(88.3, -15.1) * mm, "end": v(96.4, -15.1) * mm});
            skLineSegment(sketch, "E230.top", {"start": v(88.3, -19.2) * mm, "end": v(96.4, -19.2) * mm});
            skLineSegment(sketch, "E230.left", {"start": v(88.3, -15.1) * mm, "end": v(88.3, -19.2) * mm});
            skLineSegment(sketch, "E230.right", {"start": v(96.4, -15.1) * mm, "end": v(96.4, -19.2) * mm});
            skLineSegment(sketch, "E231.MirrorCS", {"start": v(96.4, 15.1) * mm, "end": v(96.4, 19.2) * mm});
            skLineSegment(sketch, "E232.MirrorCS", {"start": v(88.3, 15.1) * mm, "end": v(88.3, 19.2) * mm});
            skLineSegment(sketch, "E233.MirrorCS", {"start": v(88.3, 15.1) * mm, "end": v(96.4, 15.1) * mm});
            skLineSegment(sketch, "E234.MirrorCS", {"start": v(88.3, 19.2) * mm, "end": v(96.4, 19.2) * mm});
            skSolve(sketch);
        }
        {
            var Q0;
            Q0 = qSketchRegion(id + "F4", true);
            extrude(context, id + "F5", {"entities" : qUnion([Q0]), "operationType" : NewBodyOperationType.REMOVE, "endBound" : BoundingType.UP_TO_NEXT, "oppositeDirection" : true, "depth" : 25 * mm});
        }
        {
            var Q0;
            Q0=qCreatedBy(makeId("Top.planeOp"),FACE);
            var sketch = newSketch(context, id + "F6", { "sketchPlane" : qUnion([Q0])});
            skCircle(sketch, "E235.cCircle", {"center": v(-165.06, -77.98) * mm, "radius": 2.3 * mm, "construction": true});
            skLineSegment(sketch, "E235.0", {"start": v(-163.73, -80.28) * mm, "end": v(-166.38, -80.28) * mm});
            skLineSegment(sketch, "E235.1", {"start": v(-166.38, -80.28) * mm, "end": v(-167.71, -77.98) * mm});
            skLineSegment(sketch, "E235.2", {"start": v(-167.71, -77.98) * mm, "end": v(-166.38, -75.68) * mm});
            skLineSegment(sketch, "E235.3", {"start": v(-166.38, -75.68) * mm, "end": v(-163.73, -75.68) * mm});
            skLineSegment(sketch, "E235.4", {"start": v(-163.73, -75.68) * mm, "end": v(-162.4, -77.98) * mm});
            skLineSegment(sketch, "E235.5", {"start": v(-162.4, -77.98) * mm, "end": v(-163.73, -80.28) * mm});
            skPoint(sketch, "E235.0.midPoint", {"position": v(-165.06, -80.28) * mm});
            skCircle(sketch, "E236", {"center": v(-165.06, -77.98) * mm, "radius": 1.14 * mm});
            skSolve(sketch);
        }
        {
            var Q0;
            Q0=makeQuery(id+"F6.imprint","IMPRINT",FACE,{"disambiguationData":[TD([[makeQuery(id+"F6.imprint","IMPRINT",EDGE,{"derivedFrom":sQuery(id+"F6.wireOp",EDGE,"E235.0")}),-1.0]])]});
            extrude(context, id + "F7", {"entities" : qUnion([Q0]), "depth" : 30 * mm});
        }
    });
